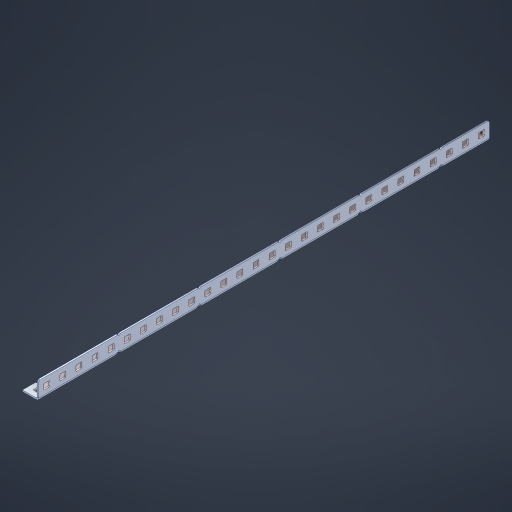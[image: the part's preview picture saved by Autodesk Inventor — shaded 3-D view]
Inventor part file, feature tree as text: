
AUTODESK INVENTOR PART (.ipt)
format: ipt  version: 2023 (Build 270158000, 158)  size: 1,154,560 bytes
history: native  units: in
note: dims shown in document units (in); Inventor stores cm internally (conversion verified against a paired STEP export)
features: other x91, extrude x82, sheet_metal_op x11, sketch x10, pattern_linear x2, mirror x1, chamfer x1
ambient origin geometry x8: Origin, YZ Plane, XZ Plane, XY Plane, X Axis, Y Axis, Z Axis, Center Point
bodies: Solid1 (feature_tree), Body (feature_tree)
feature tree (198):
  sheet_metal_op  "Flanges"
  other  "Flange Pattern Plane"
  other  "Flange Pattern Sketch"
  sheet_metal_op  "Flange Pattern"
  sheet_metal_op  "Body Pattern"
  pattern_linear  "Center Pattern"  Spacing1=0.0469in  [1 undecoded]
  other  "Arc Length"
  mirror  "Notch Mirror"
  pattern_linear  "Notch Pattern"  Spacing1=0.182in  [1 undecoded]
  chamfer  "End Chamfer"
  extrude  "Half Cut"  Depth=0.02in
  sketch  "Sketch1"  dims[d0=1.0in]
  other  "Plate1"
  sketch  "Sketch2"  dims[d1=14.0in]
  other  "Plate2"
  sheet_metal_op  "Bend1"
  sheet_metal_op  "Corner1"
  sketch  "Sketch3"  dims[d2=0.0469in]
  sketch  "Sketch7"  dims[d3=0.0469in]
  other  "Srf1"
  other  "Srf2"
  sketch  "Sketch8"  dims[d4=0.0234in]
  sketch  "Sketch9"  dims[d5=0.0938in]
  other  "Srf91"
  sheet_metal_op  "Body Pattern Sketch"
  other  "Srf92"
  sketch  "Sketch13"  dims[d6=0.0469in]
  sketch  "Sketch14"  dims[d7=0.5in d8=90.0deg d9=0.0312in]
  sketch  "Sketch15"  dims[d10=0.1875in]
  sketch  "Sketch16"  dims[d11=0.0469in d12=0.0469in d16=0.182in d17=0.02in d18=0.0469in d19=0.0in d20=0.25in d21=0.25in d38=11.0236in d40=0.5in d41=0.3937in d43=1.0in d46=0.172in d47=1.0in d48=0.0in d49=0.182in d50=0.02in d51=0.25in d52=0.25in d53=0.0469in d54=0.0in d55=0.172in d56=1.0in d57=0.0in d58=0.25in d60=11.0236in d62=0.5in d63=0.3937in d65=0.5in d85=0.1227in d86=0.1659in d88=0.04in d89=0.0469in d90=0.0in d91=0.04in d92=0.0491in d95=2.5in d96=0.04in d97=0.25in d98=45.0deg d99=0.25in d100=0.5in d101=0.0in d102=2.497in d106=0.182in d107=0.02in d108=0.5in d109=0.5in d110=0.0469in d111=0.0in d112=0.172in d113=0.5in d114=0.0in d117=0.5in d118=0.5in d119=0.5in]
  other  "Srf786"
  other  "Srf823"
  other  "Srf824"
  other  "Srf825"
  other  "Srf826"
  other  "Srf827"
  other  "Srf828"
  other  "Srf829"
  other  "Srf856"
  other  "Srf857"
  other  "Srf858"
  other  "Srf859"
  other  "Srf860"
  other  "Srf861"
  other  "Srf862"
  other  "Srf889"
  other  "Srf890"
  other  "Srf891"
  other  "Srf892"
  other  "Srf893"
  other  "Srf894"
  other  "Srf895"
  other  "Srf896"
  other  "Srf922"
  other  "Srf923"
  other  "Srf924"
  other  "Srf925"
  other  "Srf926"
  other  "Srf959"
  other  "Srf960"
  other  "Srf961"
  other  "Srf962"
  other  "Srf963"
  other  "Srf996"
  other  "Srf997"
  other  "Srf998"
  other  "Srf999"
  other  "Srf1000"
  other  "Srf1143"
  other  "Srf1144"
  other  "Srf1145"
  other  "Srf1146"
  other  "Srf1147"
  other  "Srf1148"
  other  "Srf1149"
  other  "Srf1150"
  other  "Srf1151"
  other  "Srf1152"
  other  "Srf1153"
  other  "Srf1154"
  other  "Srf1155"
  other  "Srf1156"
  other  "Srf1199"
  other  "Srf1200"
  other  "Srf1201"
  other  "Srf1202"
  other  "Srf1203"
  other  "Srf1204"
  other  "Srf1205"
  other  "Srf1206"
  other  "Srf1207"
  other  "Srf1208"
  other  "Srf1209"
  other  "Srf1210"
  other  "Srf1211"
  other  "Srf1212"
  other  "Srf1255"
  other  "Srf1256"
  other  "Srf1257"
  other  "Srf1258"
  other  "Srf1259"
  other  "Srf1260"
  other  "Srf1261"
  other  "Srf1262"
  other  "Srf1263"
  other  "Srf1264"
  other  "Srf1265"
  other  "Srf1266"
  other  "Srf1267"
  other  "Srf1268"
  sheet_metal_op  "Flange Stamp"
  sheet_metal_op  "Flange Circle"
  sheet_metal_op  "Body Stamp"
  sheet_metal_op  "Body Circle"
  other  "Center Stamp"
  other  "Center Circle"
  sheet_metal_op  "Notch"
  extrude  "ExtrusionSrf2"  Depth=0.0469in
  extrude  "ExtrusionSrf92"  TaperAngle=0.0deg  [1 undecoded]
  extrude  "ExtrusionSrf823"  Depth=0.25in
  extrude  "ExtrusionSrf824"  Depth=0.25in
  extrude  "ExtrusionSrf825"  Depth=0.5in
  extrude  "ExtrusionSrf826"  Depth=0.5in
  extrude  "ExtrusionSrf827"  Depth=1.0in TaperAngle=0.0deg
  extrude  "ExtrusionSrf828"  Depth=0.182in
  extrude  "ExtrusionSrf829"  Depth=0.02in
  extrude  "ExtrusionSrf856"  Depth=0.25in
  extrude  "ExtrusionSrf857"  Depth=0.25in
  extrude  "ExtrusionSrf858"  Depth=0.0469in
  extrude  "ExtrusionSrf859"  TaperAngle=0.0deg  [1 undecoded]
  extrude  "ExtrusionSrf860"  Depth=0.5in
  extrude  "ExtrusionSrf861"  Depth=1.0in TaperAngle=0.0deg
  extrude  "ExtrusionSrf862"  Depth=0.25in
  extrude  "ExtrusionSrf889"  Depth=0.5in
  extrude  "ExtrusionSrf890"  Depth=0.5in
  extrude  "ExtrusionSrf891"  Depth=0.5in
  extrude  "ExtrusionSrf892"  Depth=0.5in
  extrude  "ExtrusionSrf893"  Depth=0.5in
  extrude  "ExtrusionSrf894"  Depth=0.0469in
  extrude  "ExtrusionSrf895"  TaperAngle=0.0deg  [1 undecoded]
  extrude  "ExtrusionSrf896"  Depth=0.5in
  extrude  "ExtrusionSrf922"  Depth=0.5in
  extrude  "ExtrusionSrf923"  Depth=2.5in
  extrude  "ExtrusionSrf924"  Depth=0.25in TaperAngle=45.0deg
  extrude  "ExtrusionSrf925"  Depth=0.25in
  extrude  "ExtrusionSrf926"  Depth=0.5in TaperAngle=0.0deg
  extrude  "ExtrusionSrf959"  Depth=0.5in
  extrude  "ExtrusionSrf960"  Depth=0.182in
  extrude  "ExtrusionSrf961"  Depth=0.02in
  extrude  "ExtrusionSrf962"  Depth=0.5in
  extrude  "ExtrusionSrf963"  Depth=0.5in
  extrude  "ExtrusionSrf996"  Depth=0.0469in
  extrude  "ExtrusionSrf997"  TaperAngle=0.0deg  [1 undecoded]
  extrude  "ExtrusionSrf998"  Depth=0.5in
  extrude  "ExtrusionSrf999"  Depth=0.5in TaperAngle=0.0deg
  extrude  "ExtrusionSrf1000"  Depth=0.5in
  extrude  "ExtrusionSrf1143"  Depth=0.5in
  extrude  "ExtrusionSrf1144"  Depth=0.5in
  extrude  "ExtrusionSrf1145"  [1 undecoded]
  extrude  "ExtrusionSrf1146"  [1 undecoded]
  extrude  "ExtrusionSrf1147"  [1 undecoded]
  extrude  "ExtrusionSrf1148"  [1 undecoded]
  extrude  "ExtrusionSrf1149"  [1 undecoded]
  extrude  "ExtrusionSrf1150"  [1 undecoded]
  extrude  "ExtrusionSrf1151"  [1 undecoded]
  extrude  "ExtrusionSrf1152"  [1 undecoded]
  extrude  "ExtrusionSrf1153"  [1 undecoded]
  extrude  "ExtrusionSrf1154"  [1 undecoded]
  extrude  "ExtrusionSrf1155"  [1 undecoded]
  extrude  "ExtrusionSrf1156"  [1 undecoded]
  extrude  "ExtrusionSrf1199"  [1 undecoded]
  extrude  "ExtrusionSrf1200"  [1 undecoded]
  extrude  "ExtrusionSrf1201"  [1 undecoded]
  extrude  "ExtrusionSrf1202"  [1 undecoded]
  extrude  "ExtrusionSrf1203"  [1 undecoded]
  extrude  "ExtrusionSrf1204"  [1 undecoded]
  extrude  "ExtrusionSrf1205"  [1 undecoded]
  extrude  "ExtrusionSrf1206"  [1 undecoded]
  extrude  "ExtrusionSrf1207"  [1 undecoded]
  extrude  "ExtrusionSrf1208"  [1 undecoded]
  extrude  "ExtrusionSrf1209"  [1 undecoded]
  extrude  "ExtrusionSrf1210"  [1 undecoded]
  extrude  "ExtrusionSrf1211"  [1 undecoded]
  extrude  "ExtrusionSrf1212"  [1 undecoded]
  extrude  "ExtrusionSrf1255"  [1 undecoded]
  extrude  "ExtrusionSrf1256"  [1 undecoded]
  extrude  "ExtrusionSrf1257"  [1 undecoded]
  extrude  "ExtrusionSrf1258"  [1 undecoded]
  extrude  "ExtrusionSrf1259"  [1 undecoded]
  extrude  "ExtrusionSrf1260"  [1 undecoded]
  extrude  "ExtrusionSrf1261"  [1 undecoded]
  extrude  "ExtrusionSrf1262"  [1 undecoded]
  extrude  "ExtrusionSrf1263"  [1 undecoded]
  extrude  "ExtrusionSrf1264"  [1 undecoded]
  extrude  "ExtrusionSrf1265"  [1 undecoded]
  extrude  "ExtrusionSrf1266"  [1 undecoded]
  extrude  "ExtrusionSrf1267"  [1 undecoded]
  extrude  "ExtrusionSrf1268"  [1 undecoded]
note: 46 required parameter values undecoded (feature->parameter linkage not recoverable at this tier; creation-order binding heuristic only, values carry confidence <= 0.55)
